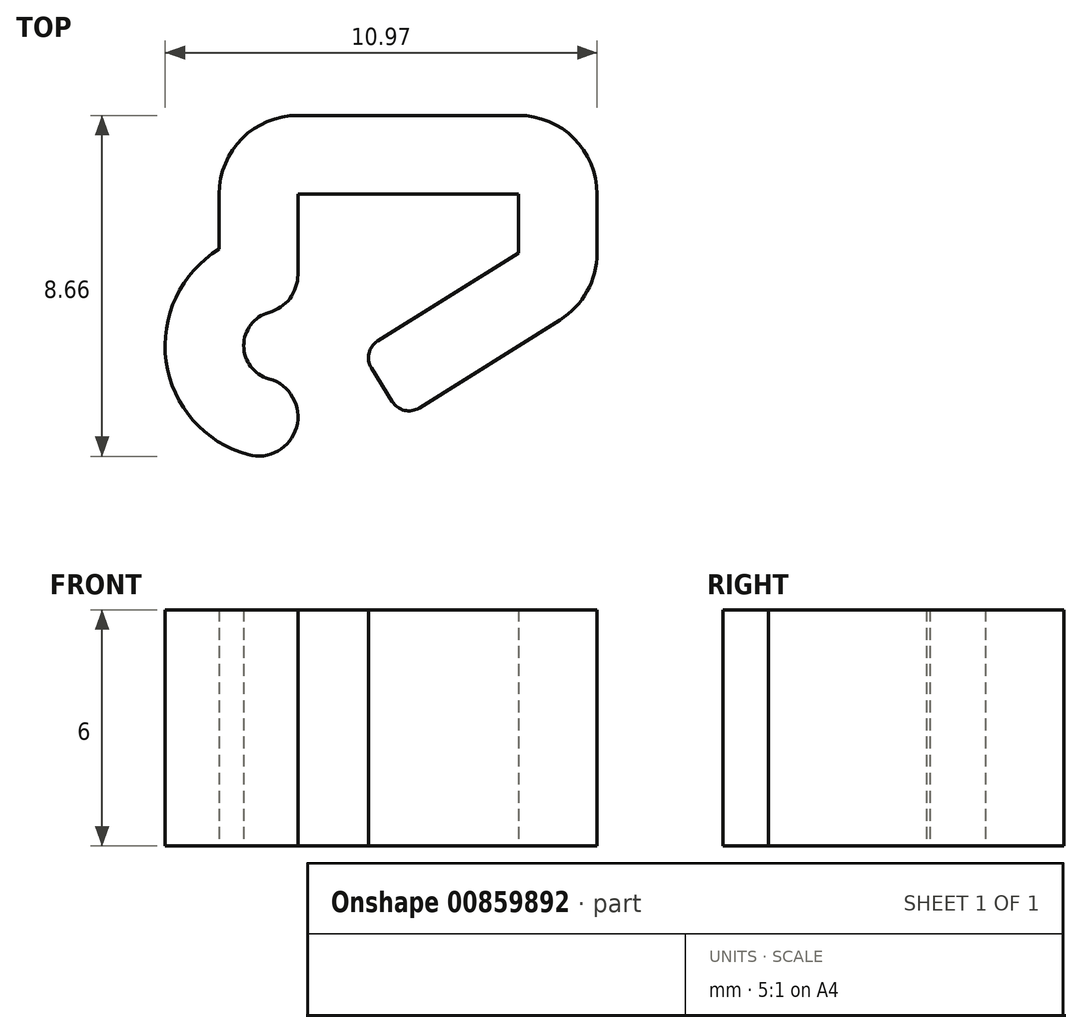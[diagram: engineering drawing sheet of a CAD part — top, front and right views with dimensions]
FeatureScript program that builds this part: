
annotation { "Feature Type Name" : "Feature", "Feature Type Description" : "" }
export const myFeature = defineFeature(function(context is Context, id is Id, definition is map)
    precondition{}
    {
        {
            var Q0;
            Q0=qCreatedBy(makeId("Top.planeOp"),FACE);
            var sketch = newSketch(context, id + "F0", { "sketchPlane" : qUnion([Q0])});
            skCircle(sketch, "E0", {"center": v(-63.6, 20.63) * mm, "radius": 0.88 * mm, "construction": true});
            skLineSegment(sketch, "E1", {"start": v(-62.52, 21.7) * mm, "end": v(-57.02, 21.7) * mm, "construction": true});
            skLineSegment(sketch, "E2", {"start": v(-57.02, 21.7) * mm, "end": v(-57.02, 17.7) * mm, "construction": true});
            skLineSegment(sketch, "E3", {"start": v(-62.52, 21.7) * mm, "end": v(-62.52, 20.17) * mm, "construction": true});
            skLineSegment(sketch, "E4", {"start": v(-57.02, 17.7) * mm, "end": v(-61.02, 17.7) * mm, "construction": true});
            skLineSegment(sketch, "E5", {"start": v(-79.37, 21.7) * mm, "end": v(-73.77, 21.7) * mm});
            skLineSegment(sketch, "E6", {"start": v(-73.77, 21.7) * mm, "end": v(-73.77, 20.2) * mm});
            skLineSegment(sketch, "E7", {"start": v(-73.77, 20.2) * mm, "end": v(-77.34, 17.97) * mm});
            skLineSegment(sketch, "E8", {"start": v(-72.7, 18.5) * mm, "end": v(-76.28, 16.27) * mm});
            skLineSegment(sketch, "E9", {"start": v(-71.77, 20.2) * mm, "end": v(-71.77, 21.7) * mm});
            skLineSegment(sketch, "E10", {"start": v(-73.77, 23.7) * mm, "end": v(-79.37, 23.7) * mm});
            skLineSegment(sketch, "E11", {"start": v(-77.5, 17.28) * mm, "end": v(-76.97, 16.43) * mm});
            skCircle(sketch, "E12", {"center": v(-79.87, 17.85) * mm, "radius": 0.88 * mm, "construction": true});
            skArc(sketch, "E13", {"start": v(-79.87, 18.73) * mm, "mid": v(-80.74, 17.85) * mm, "end": v(-79.87, 16.98) * mm});
            skPoint(sketch, "E14.visualSharp", {"position": v(-77.77, 17.7) * mm});
            skArc(sketch, "E14.filletArc", {"start": v(-77.34, 17.97) * mm, "mid": v(-77.57, 17.66) * mm, "end": v(-77.5, 17.28) * mm});
            skPoint(sketch, "E15.visualSharp", {"position": v(-76.7, 16) * mm});
            skArc(sketch, "E15.filletArc", {"start": v(-76.97, 16.43) * mm, "mid": v(-76.66, 16.2) * mm, "end": v(-76.28, 16.27) * mm});
            skPoint(sketch, "E16.visualSharp", {"position": v(-71.77, 23.7) * mm});
            skArc(sketch, "E16.filletArc", {"start": v(-71.77, 21.7) * mm, "mid": v(-72.35, 23.12) * mm, "end": v(-73.77, 23.7) * mm});
            skLineSegment(sketch, "E17", {"start": v(-79.37, 21.7) * mm, "end": v(-79.37, 18.73) * mm});
            skPoint(sketch, "E18.visualSharp", {"position": v(-81.13, 23.7) * mm});
            skArc(sketch, "E18.filletArc", {"start": v(-79.37, 23.7) * mm, "mid": v(-80.78, 23.12) * mm, "end": v(-81.37, 21.7) * mm});
            skCircle(sketch, "E19", {"center": v(-79.87, 17.85) * mm, "radius": 2.88 * mm, "construction": true});
            skArc(sketch, "E20", {"start": v(-72.7, 18.5) * mm, "mid": v(-72.02, 19.23) * mm, "end": v(-71.77, 20.2) * mm});
            skLineSegment(sketch, "E21", {"start": v(-77.77, 17.7) * mm, "end": v(-73.77, 17.7) * mm, "construction": true});
            skLineSegment(sketch, "E22", {"start": v(-73.77, 20.2) * mm, "end": v(-73.77, 17.7) * mm, "construction": true});
            skLineSegment(sketch, "E23", {"start": v(-81.37, 21.7) * mm, "end": v(-81.37, 20.3) * mm});
            skLineSegment(sketch, "E24", {"start": v(-79.87, 18.73) * mm, "end": v(-79.87, 16.98) * mm, "construction": true});
            skLineSegment(sketch, "E25", {"start": v(-79.87, 18.73) * mm, "end": v(-79.37, 18.73) * mm});
            skLineSegment(sketch, "E26", {"start": v(-79.87, 16.98) * mm, "end": v(-79.37, 16.98) * mm});
            skLineSegment(sketch, "E27", {"start": v(-79.37, 16.98) * mm, "end": v(-79.37, 15.02) * mm});
            skArc(sketch, "E28", {"start": v(-81.37, 20.3) * mm, "mid": v(-82.56, 16.83) * mm, "end": v(-79.37, 15.02) * mm});
            skSolve(sketch);
        }
        {
            var Q0;
            Q0=makeQuery(id+"F0.imprint","IMPRINT",FACE,{"disambiguationData":[TD([[makeQuery(id+"F0.imprint","IMPRINT",EDGE,{"derivedFrom":sQuery(id+"F0.wireOp",EDGE,"E5")}),1.0]])]});
            extrude(context, id + "F1", {"entities" : qUnion([Q0]), "depth" : 6 * mm, "offsetDistance" : 25 * mm});
        }
        {
            var Q0;
            Q0=makeQuery(id+"F1.opExtrude","SWEPT_EDGE",EDGE,{"disambiguationData":[OSD([sQuery(id+"F0.wireOp",EDGE,"E27"),sQuery(id+"F0.wireOp",EDGE,"E28")])]});
            var Q1;
            Q1=makeQuery(id+"F1.opExtrude","SWEPT_EDGE",EDGE,{"disambiguationData":[OSD([sQuery(id+"F0.wireOp",EDGE,"E17"),sQuery(id+"F0.wireOp",EDGE,"E25")])]});
            var Q2;
            Q2=makeQuery(id+"F1.opExtrude","SWEPT_EDGE",EDGE,{"disambiguationData":[OSD([sQuery(id+"F0.wireOp",EDGE,"E26"),sQuery(id+"F0.wireOp",EDGE,"E27")])]});
            fillet(context, id + "F2", {"entities" : qUnion([Q0, Q1, Q2]), "radius" : 1 * mm, "tangentPropagation" : true, "allowEdgeOverflow" : false});
        }
    });
